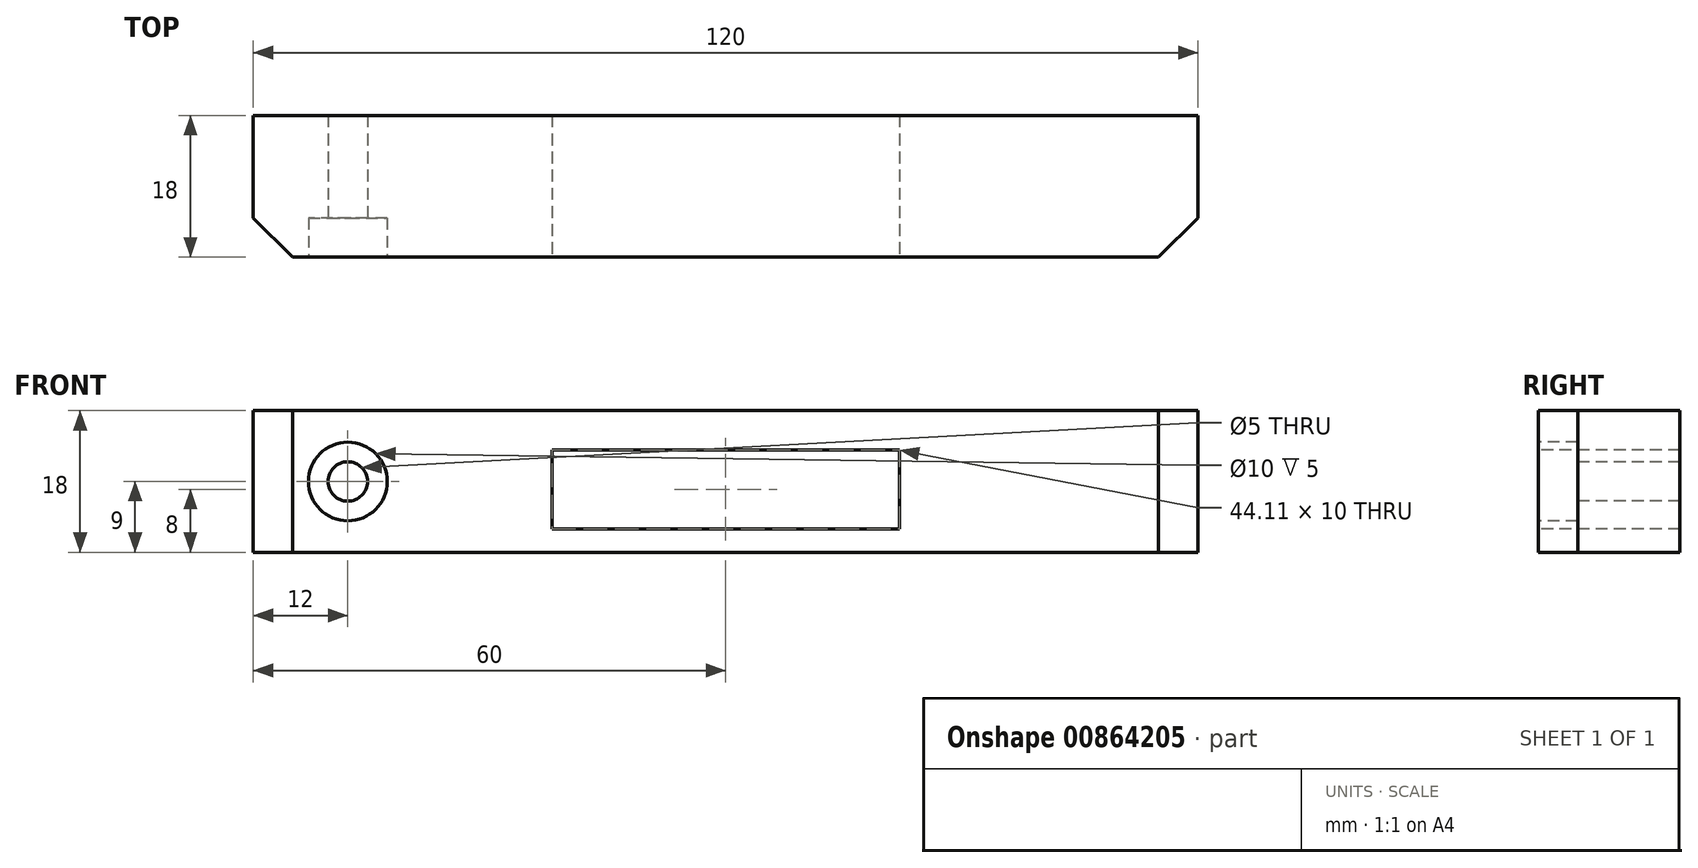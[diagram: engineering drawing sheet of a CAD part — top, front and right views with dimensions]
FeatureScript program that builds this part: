
annotation { "Feature Type Name" : "Feature", "Feature Type Description" : "" }
export const myFeature = defineFeature(function(context is Context, id is Id, definition is map)
    precondition{}
    {
        {
            var Q0;
            Q0=qCreatedBy(makeId("Top.planeOp"),FACE);
            var sketch = newSketch(context, id + "F0", { "sketchPlane" : qUnion([Q0])});
            skLineSegment(sketch, "E0.bottom", {"start": v(-60, 9) * mm, "end": v(60, 9) * mm});
            skLineSegment(sketch, "E0.top", {"start": v(-60, -9) * mm, "end": v(60, -9) * mm});
            skLineSegment(sketch, "E0.left", {"start": v(-60, 9) * mm, "end": v(-60, -9) * mm});
            skLineSegment(sketch, "E0.right", {"start": v(60, 9) * mm, "end": v(60, -9) * mm});
            skSolve(sketch);
        }
        {
            var Q0;
            Q0=makeQuery(id+"F0.imprint","IMPRINT",FACE,{"disambiguationData":[TD([[makeQuery(id+"F0.imprint","IMPRINT",EDGE,{"derivedFrom":sQuery(id+"F0.wireOp",EDGE,"E0.bottom")}),-1.0]])]});
            extrude(context, id + "F1", {"entities" : qUnion([Q0]), "endBound" : BoundingType.SYMMETRIC, "depth" : 18 * mm, "offsetDistance" : 25 * mm});
        }
        {
            var Q0;
            Q0=makeQuery(id+"F1.opExtrude","SWEPT_FACE",FACE,{"disambiguationData":[OSD([sQuery(id+"F0.wireOp",EDGE,"E0.top")])]});
            var sketch = newSketch(context, id + "F2", { "sketchPlane" : qUnion([Q0])});
            skLineSegment(sketch, "E1.bottom", {"start": v(-22.05, 4) * mm, "end": v(22.05, 4) * mm});
            skLineSegment(sketch, "E1.top", {"start": v(-22.05, -6) * mm, "end": v(22.05, -6) * mm});
            skLineSegment(sketch, "E1.left", {"start": v(-22.05, 4) * mm, "end": v(-22.05, -6) * mm});
            skLineSegment(sketch, "E1.right", {"start": v(22.05, 4) * mm, "end": v(22.05, -6) * mm});
            skSolve(sketch);
        }
        {
            var Q0;
            Q0=makeQuery(id+"F2.imprint","IMPRINT",FACE,{"disambiguationData":[TD([[makeQuery(id+"F2.imprint","IMPRINT",EDGE,{"derivedFrom":sQuery(id+"F2.wireOp",EDGE,"E1.bottom")}),-1.0]])]});
            extrude(context, id + "F3", {"entities" : qUnion([Q0]), "operationType" : NewBodyOperationType.REMOVE, "oppositeDirection" : true, "depth" : 25 * mm, "offsetDistance" : 25 * mm});
        }
        {
            var Q0;
            Q0=makeQuery(id+"F1.opExtrude","SWEPT_FACE",FACE,{"disambiguationData":[OSD([sQuery(id+"F0.wireOp",EDGE,"E0.top")])]});
            var sketch = newSketch(context, id + "F4", { "sketchPlane" : qUnion([Q0])});
            skPoint(sketch, "E2", {"position": v(-48, 0) * mm});
            skSolve(sketch);
        }
        {
            var Q0;
            Q0=sQuery(id+"F4.wireOp",VERTEX,"E2");
            var Q1;
            Q1=makeQuery(id+"F1.opExtrude","SWEPT_BODY",BODY,{"disambiguationData":[OSD([sQuery(id+"F0.wireOp",EDGE,"E0.bottom"),sQuery(id+"F0.wireOp",EDGE,"E0.top"),sQuery(id+"F0.wireOp",EDGE,"E0.left"),sQuery(id+"F0.wireOp",EDGE,"E0.right")])]});
            hole(context, id + "F5", {"style" : HoleStyle.C_BORE, "endStyle" : HoleEndStyle.THROUGH, "holeDiameter" : 5 * mm, "cBoreDiameter" : 10 * mm, "cBoreDepth" : 5 * mm, "majorDiameter" : 5 * mm, "isTappedThrough" : true, "tappedDepth" : 12 * mm, "tapClearance" : 3, "locations" : qUnion([Q0]), "scope" : qUnion([Q1])});
        }
        {
            var Q0;
            Q0=makeQuery(id+"F1.opExtrude","SWEPT_EDGE",EDGE,{"disambiguationData":[OSD([sQuery(id+"F0.wireOp",EDGE,"E0.top"),sQuery(id+"F0.wireOp",EDGE,"E0.right")])]});
            var Q1;
            Q1=makeQuery(id+"F1.opExtrude","SWEPT_EDGE",EDGE,{"disambiguationData":[OSD([sQuery(id+"F0.wireOp",EDGE,"E0.top"),sQuery(id+"F0.wireOp",EDGE,"E0.left")])]});
            chamfer(context, id + "F6", {"entities" : qUnion([Q0, Q1]), "width" : 5 * mm, "tangentPropagation" : true});
        }
    });
